# Revit family: A481408S
name_source: partatom
category: Mechanical Equipment
revit_build: Autodesk Revit MEP 2016 (Build: 20150220_1215(x64)
units: mm (PartAtom-declared; Revit-internal decimal feet)

## family parameters
Cut with Voids When Loaded = No
Host = Face
OmniClass Number = 23.65.70.14.11
OmniClass Title = Drinking Fountains/Coolers
Part Type = Normal
Room Calculation Point = No
Round Connector Dimension = Use Diameter
Shared = Yes

## types (1)
- A481408S
    220V- 220 vot / 50 Hz compressor = Yes
    A481408F - Flexible Bubbler = No
    A481408S - Stainless Steel Bubbler = Yes
    Amperage = 0
    CW Connection = Yes
    Default Elevation = 51.687 "
    Description = Fully Recessed Wall Mounted Electric Drinking Fountain
    GF2- Glass Filler = Yes
    HW Connection = No
    Manufacturer = Murdock
    Material = Stainless Steel
    Model = A481408S
    OVERALL DEPTH = 10
    OVERALL SIZE HEIGHT = 56.75
    OVERALL SIZE WIDTH = 19
    Revised Date = 03/24/20
    Tempered Water Connection = No
    URL = https://www.murdockmfg.com
    Vent Connection = No
    Voltage = 0
    WF1- 1500 Gallon Capacity, NSF 42+53, 1 micron lead reduction filter = Yes
    Waste Connection = Yes

## geometry (parser evidence)
native form markers: Sweep x8
no freeform markers — native parametric forms only
